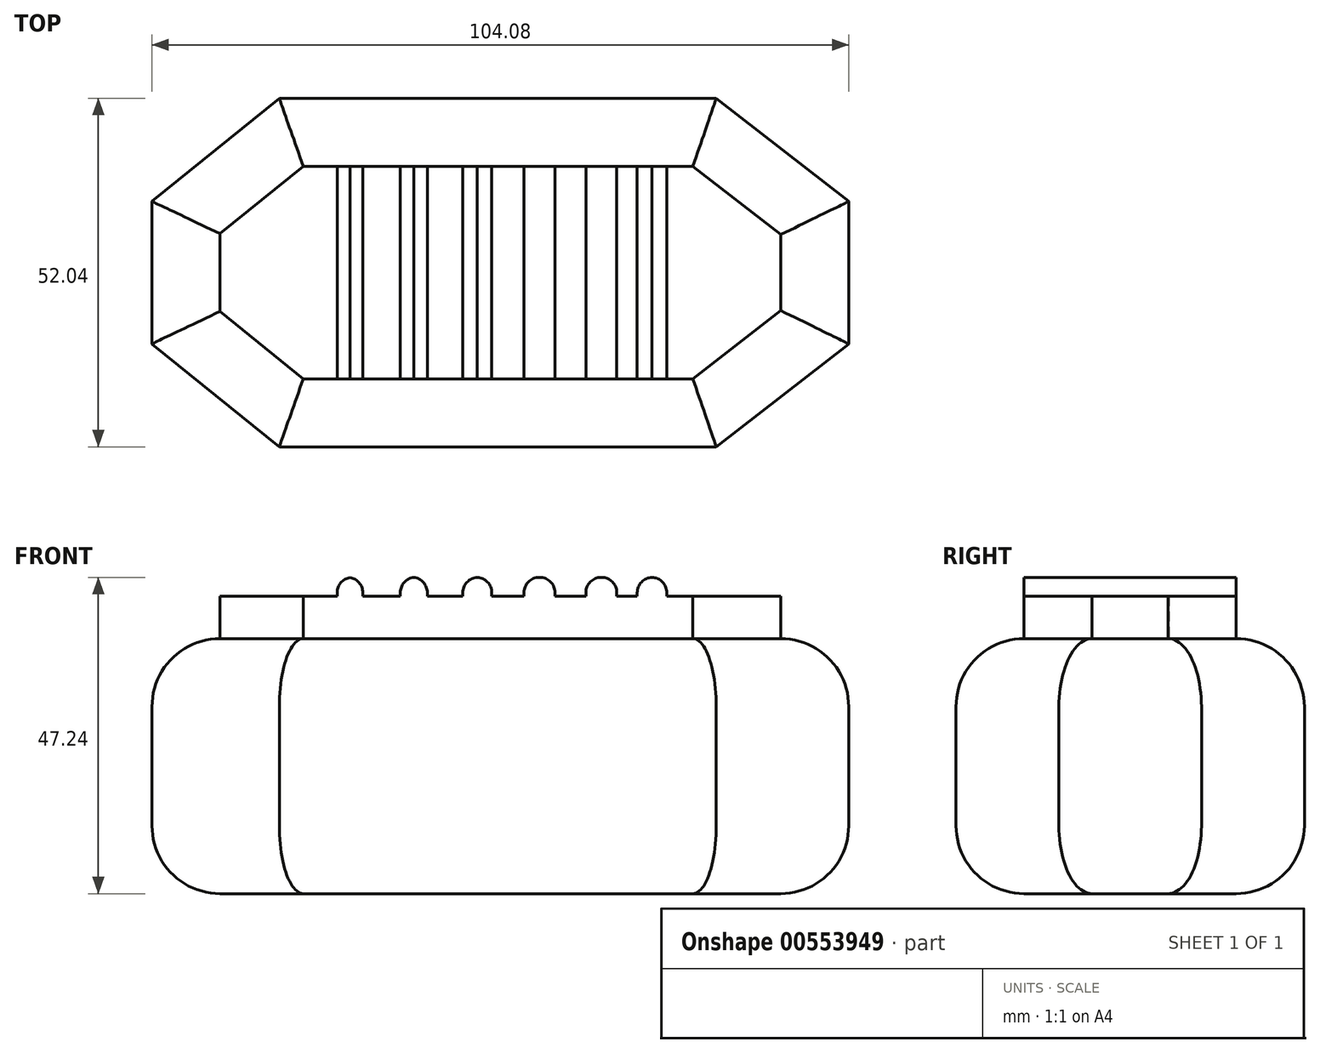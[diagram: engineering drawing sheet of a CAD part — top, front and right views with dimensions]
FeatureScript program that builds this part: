
annotation { "Feature Type Name" : "Feature", "Feature Type Description" : "" }
export const myFeature = defineFeature(function(context is Context, id is Id, definition is map)
    precondition{}
    {
        {
            var Q0;
            Q0=qCreatedBy(makeId("Top.planeOp"),FACE);
            var sketch = newSketch(context, id + "F0", { "sketchPlane" : qUnion([Q0])});
            skLineSegment(sketch, "E0.bottom", {"start": v(52.04, -26.02) * mm, "end": v(-52.04, -26.02) * mm});
            skLineSegment(sketch, "E0.top", {"start": v(52.04, 26.02) * mm, "end": v(-52.04, 26.02) * mm});
            skLineSegment(sketch, "E0.left", {"start": v(52.04, -26.02) * mm, "end": v(52.04, 26.02) * mm});
            skLineSegment(sketch, "E0.right", {"start": v(-52.04, -26.02) * mm, "end": v(-52.04, 26.02) * mm});
            skPoint(sketch, "E0.middle", {"position": v(0, 0) * mm});
            skLineSegment(sketch, "E1", {"start": v(-33.02, -26.02) * mm, "end": v(-52.04, -10.65) * mm});
            skLineSegment(sketch, "E2", {"start": v(-33.02, 26.02) * mm, "end": v(-52.04, 10.65) * mm});
            skLineSegment(sketch, "E3", {"start": v(52.04, 10.65) * mm, "end": v(32.23, 26.02) * mm});
            skLineSegment(sketch, "E4", {"start": v(52.04, -10.65) * mm, "end": v(32.23, -26.02) * mm});
            skSolve(sketch);
        }
        {
            var Q0;
            {var subQ0=sQuery(id+"F0.wireOp",EDGE,"E1");Q0=makeQuery(id+"F0.imprint","IMPRINT",FACE,{"disambiguationData":[TD([[makeQuery(id+"F0.imprint","IMPRINT",EDGE,{"derivedFrom":subQ0}),-1.0]])]});}
            extrude(context, id + "F1", {"entities" : qUnion([Q0]), "depth" : 38.1 * mm, "offsetDistance" : 25.4 * mm});
        }
        {
            var Q0;
            Q0=makeQuery(id+"F1.opExtrude","CAP_EDGE",EDGE,{"disambiguationData":[OSD([sQuery(id+"F0.wireOp",EDGE,"E0.bottom")])],"isStart":false});
            var Q1;
            Q1=makeQuery(id+"F1.opExtrude","CAP_EDGE",EDGE,{"disambiguationData":[OSD([sQuery(id+"F0.wireOp",EDGE,"E1")])],"isStart":false});
            var Q2;
            Q2=makeQuery(id+"F1.opExtrude","CAP_EDGE",EDGE,{"disambiguationData":[OSD([sQuery(id+"F0.wireOp",EDGE,"E0.right")])],"isStart":false});
            var Q3;
            Q3=makeQuery(id+"F1.opExtrude","CAP_EDGE",EDGE,{"disambiguationData":[OSD([sQuery(id+"F0.wireOp",EDGE,"E2")])],"isStart":false});
            var Q4;
            Q4=makeQuery(id+"F1.opExtrude","CAP_EDGE",EDGE,{"disambiguationData":[OSD([sQuery(id+"F0.wireOp",EDGE,"E0.top")])],"isStart":false});
            var Q5;
            Q5=makeQuery(id+"F1.opExtrude","CAP_EDGE",EDGE,{"disambiguationData":[OSD([sQuery(id+"F0.wireOp",EDGE,"E3")])],"isStart":false});
            var Q6;
            Q6=makeQuery(id+"F1.opExtrude","CAP_EDGE",EDGE,{"disambiguationData":[OSD([sQuery(id+"F0.wireOp",EDGE,"E0.left")])],"isStart":false});
            var Q7;
            Q7=makeQuery(id+"F1.opExtrude","CAP_EDGE",EDGE,{"disambiguationData":[OSD([sQuery(id+"F0.wireOp",EDGE,"E4")])],"isStart":false});
            fillet(context, id + "F2", {"entities" : qUnion([Q0, Q1, Q2, Q3, Q4, Q5, Q6, Q7]), "radius" : 10.16 * mm, "tangentPropagation" : true, "allowEdgeOverflow" : false});
        }
        {
            var Q0;
            Q0=makeQuery(id+"F1.opExtrude","CAP_EDGE",EDGE,{"disambiguationData":[OSD([sQuery(id+"F0.wireOp",EDGE,"E0.bottom")])],"isStart":true});
            var Q1;
            Q1=makeQuery(id+"F1.opExtrude","CAP_EDGE",EDGE,{"disambiguationData":[OSD([sQuery(id+"F0.wireOp",EDGE,"E1")])],"isStart":true});
            var Q2;
            Q2=makeQuery(id+"F1.opExtrude","CAP_EDGE",EDGE,{"disambiguationData":[OSD([sQuery(id+"F0.wireOp",EDGE,"E0.right")])],"isStart":true});
            var Q3;
            Q3=makeQuery(id+"F1.opExtrude","CAP_EDGE",EDGE,{"disambiguationData":[OSD([sQuery(id+"F0.wireOp",EDGE,"E2")])],"isStart":true});
            var Q4;
            Q4=makeQuery(id+"F1.opExtrude","CAP_EDGE",EDGE,{"disambiguationData":[OSD([sQuery(id+"F0.wireOp",EDGE,"E0.top")])],"isStart":true});
            var Q5;
            Q5=makeQuery(id+"F1.opExtrude","CAP_EDGE",EDGE,{"disambiguationData":[OSD([sQuery(id+"F0.wireOp",EDGE,"E3")])],"isStart":true});
            var Q6;
            Q6=makeQuery(id+"F1.opExtrude","CAP_EDGE",EDGE,{"disambiguationData":[OSD([sQuery(id+"F0.wireOp",EDGE,"E0.left")])],"isStart":true});
            var Q7;
            Q7=makeQuery(id+"F1.opExtrude","CAP_EDGE",EDGE,{"disambiguationData":[OSD([sQuery(id+"F0.wireOp",EDGE,"E4")])],"isStart":true});
            fillet(context, id + "F3", {"entities" : qUnion([Q0, Q1, Q2, Q3, Q4, Q5, Q6, Q7]), "radius" : 10.16 * mm, "tangentPropagation" : true, "allowEdgeOverflow" : false});
        }
        {
            var Q0;
            Q0=makeQuery(id+"F1.opExtrude","CAP_FACE",FACE,{"disambiguationData":[OSD([sQuery(id+"F0.wireOp",EDGE,"E0.bottom"),sQuery(id+"F0.wireOp",EDGE,"E0.top"),sQuery(id+"F0.wireOp",EDGE,"E0.left"),sQuery(id+"F0.wireOp",EDGE,"E0.right"),sQuery(id+"F0.wireOp",EDGE,"E1"),sQuery(id+"F0.wireOp",EDGE,"E2"),sQuery(id+"F0.wireOp",EDGE,"E3"),sQuery(id+"F0.wireOp",EDGE,"E4")])],"isStart":false});
            var sketch = newSketch(context, id + "F4", { "sketchPlane" : qUnion([Q0])});
            skLineSegment(sketch, "E5", {"start": v(-41.88, 5.8) * mm, "end": v(-29.43, 15.86) * mm});
            skLineSegment(sketch, "E6", {"start": v(-29.43, 15.86) * mm, "end": v(28.75, 15.86) * mm});
            skLineSegment(sketch, "E7", {"start": v(28.75, 15.86) * mm, "end": v(41.88, 5.68) * mm});
            skLineSegment(sketch, "E8", {"start": v(41.88, 5.68) * mm, "end": v(41.88, -5.67) * mm});
            skLineSegment(sketch, "E9", {"start": v(41.88, -5.67) * mm, "end": v(28.75, -15.86) * mm});
            skLineSegment(sketch, "E10", {"start": v(28.75, -15.86) * mm, "end": v(-29.43, -15.86) * mm});
            skLineSegment(sketch, "E11", {"start": v(-29.43, -15.86) * mm, "end": v(-41.88, -5.8) * mm});
            skLineSegment(sketch, "E12", {"start": v(-41.88, -5.8) * mm, "end": v(-41.88, 5.8) * mm});
            skSolve(sketch);
        }
        {
            var Q0;
            Q0 = qSketchRegion(id + "F4", true);
            extrude(context, id + "F5", {"entities" : qUnion([Q0]), "operationType" : NewBodyOperationType.ADD, "depth" : 6.35 * mm, "offsetDistance" : 25.4 * mm});
        }
        {
            var Q0;
            Q0=makeQuery(id+"F5.opExtrude","CAP_FACE",FACE,{"disambiguationData":[OSD([sQuery(id+"F4.wireOp",EDGE,"E5"),sQuery(id+"F4.wireOp",EDGE,"E6"),sQuery(id+"F4.wireOp",EDGE,"E7"),sQuery(id+"F4.wireOp",EDGE,"E8"),sQuery(id+"F4.wireOp",EDGE,"E9"),sQuery(id+"F4.wireOp",EDGE,"E10"),sQuery(id+"F4.wireOp",EDGE,"E11"),sQuery(id+"F4.wireOp",EDGE,"E12")])],"isStart":false});
            var sketch = newSketch(context, id + "F6", { "sketchPlane" : qUnion([Q0])});
            skLineSegment(sketch, "E13.bottom", {"start": v(-24.37, -15.86) * mm, "end": v(-20.54, -15.86) * mm});
            skLineSegment(sketch, "E13.top", {"start": v(-24.37, 15.86) * mm, "end": v(-20.54, 15.86) * mm});
            skLineSegment(sketch, "E13.left", {"start": v(-24.37, -15.86) * mm, "end": v(-24.37, 15.86) * mm});
            skLineSegment(sketch, "E13.right", {"start": v(-20.54, -15.86) * mm, "end": v(-20.54, 15.86) * mm});
            skLineSegment(sketch, "E14.bottom", {"start": v(-14.94, 15.86) * mm, "end": v(-10.9, 15.86) * mm});
            skLineSegment(sketch, "E14.top", {"start": v(-14.94, -15.86) * mm, "end": v(-10.9, -15.86) * mm});
            skLineSegment(sketch, "E14.left", {"start": v(-14.94, 15.86) * mm, "end": v(-14.94, -15.86) * mm});
            skLineSegment(sketch, "E14.right", {"start": v(-10.9, 15.86) * mm, "end": v(-10.9, -15.86) * mm});
            skLineSegment(sketch, "E15.bottom", {"start": v(-5.6, -15.86) * mm, "end": v(-1.28, -15.86) * mm});
            skLineSegment(sketch, "E15.top", {"start": v(-5.6, 15.86) * mm, "end": v(-1.28, 15.86) * mm});
            skLineSegment(sketch, "E15.left", {"start": v(-5.6, -15.86) * mm, "end": v(-5.6, 15.86) * mm});
            skLineSegment(sketch, "E15.right", {"start": v(-1.28, -15.86) * mm, "end": v(-1.28, 15.86) * mm});
            skLineSegment(sketch, "E16.bottom", {"start": v(3.54, 15.86) * mm, "end": v(8.16, 15.86) * mm});
            skLineSegment(sketch, "E16.top", {"start": v(3.54, -15.86) * mm, "end": v(8.16, -15.86) * mm});
            skLineSegment(sketch, "E16.left", {"start": v(3.54, 15.86) * mm, "end": v(3.54, -15.86) * mm});
            skLineSegment(sketch, "E16.right", {"start": v(8.16, 15.86) * mm, "end": v(8.16, -15.86) * mm});
            skLineSegment(sketch, "E17.bottom", {"start": v(12.78, -15.86) * mm, "end": v(17.4, -15.86) * mm});
            skLineSegment(sketch, "E17.top", {"start": v(12.78, 15.86) * mm, "end": v(17.4, 15.86) * mm});
            skLineSegment(sketch, "E17.left", {"start": v(12.78, -15.86) * mm, "end": v(12.78, 15.86) * mm});
            skLineSegment(sketch, "E17.right", {"start": v(17.4, -15.86) * mm, "end": v(17.4, 15.86) * mm});
            skLineSegment(sketch, "E18.bottom", {"start": v(20.44, -15.86) * mm, "end": v(24.86, -15.86) * mm});
            skLineSegment(sketch, "E18.top", {"start": v(20.44, 15.86) * mm, "end": v(24.86, 15.86) * mm});
            skLineSegment(sketch, "E18.left", {"start": v(20.44, -15.86) * mm, "end": v(20.44, 15.86) * mm});
            skLineSegment(sketch, "E18.right", {"start": v(24.86, -15.86) * mm, "end": v(24.86, 15.86) * mm});
            skSolve(sketch);
        }
        {
            var Q0;
            Q0 = qSketchRegion(id + "F6", true);
            extrude(context, id + "F7", {"entities" : qUnion([Q0]), "operationType" : NewBodyOperationType.ADD, "depth" : 2.8 * mm, "offsetDistance" : 25.4 * mm});
        }
        {
            var Q0;
            Q0=makeQuery(id+"F7.opExtrude","CAP_EDGE",EDGE,{"disambiguationData":[OSD([sQuery(id+"F6.wireOp",EDGE,"E13.right")])],"isStart":false});
            var Q1;
            Q1=makeQuery(id+"F7.opExtrude","CAP_EDGE",EDGE,{"disambiguationData":[OSD([sQuery(id+"F6.wireOp",EDGE,"E14.right")])],"isStart":false});
            var Q2;
            Q2=makeQuery(id+"F7.opExtrude","CAP_EDGE",EDGE,{"disambiguationData":[OSD([sQuery(id+"F6.wireOp",EDGE,"E15.right")])],"isStart":false});
            var Q3;
            Q3=makeQuery(id+"F7.opExtrude","CAP_EDGE",EDGE,{"disambiguationData":[OSD([sQuery(id+"F6.wireOp",EDGE,"E16.right")])],"isStart":false});
            var Q4;
            Q4=makeQuery(id+"F7.opExtrude","CAP_EDGE",EDGE,{"disambiguationData":[OSD([sQuery(id+"F6.wireOp",EDGE,"E17.right")])],"isStart":false});
            var Q5;
            Q5=makeQuery(id+"F7.opExtrude","CAP_EDGE",EDGE,{"disambiguationData":[OSD([sQuery(id+"F6.wireOp",EDGE,"E18.right")])],"isStart":false});
            var Q6;
            Q6=makeQuery(id+"F7.opExtrude","CAP_EDGE",EDGE,{"disambiguationData":[OSD([sQuery(id+"F6.wireOp",EDGE,"E18.left")])],"isStart":false});
            var Q7;
            Q7=makeQuery(id+"F7.opExtrude","CAP_EDGE",EDGE,{"disambiguationData":[OSD([sQuery(id+"F6.wireOp",EDGE,"E17.left")])],"isStart":false});
            var Q8;
            Q8=makeQuery(id+"F7.opExtrude","CAP_EDGE",EDGE,{"disambiguationData":[OSD([sQuery(id+"F6.wireOp",EDGE,"E16.left")])],"isStart":false});
            var Q9;
            Q9=makeQuery(id+"F7.opExtrude","CAP_EDGE",EDGE,{"disambiguationData":[OSD([sQuery(id+"F6.wireOp",EDGE,"E15.left")])],"isStart":false});
            var Q10;
            Q10=makeQuery(id+"F7.opExtrude","CAP_EDGE",EDGE,{"disambiguationData":[OSD([sQuery(id+"F6.wireOp",EDGE,"E14.left")])],"isStart":false});
            var Q11;
            Q11=makeQuery(id+"F7.opExtrude","CAP_EDGE",EDGE,{"disambiguationData":[OSD([sQuery(id+"F6.wireOp",EDGE,"E13.left")])],"isStart":false});
            fillet(context, id + "F8", {"entities" : qUnion([Q0, Q1, Q2, Q3, Q4, Q5, Q6, Q7, Q8, Q9, Q10, Q11]), "radius" : 2.3 * mm, "tangentPropagation" : true, "allowEdgeOverflow" : false});
        }
    });
